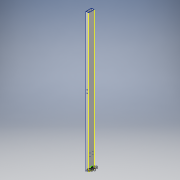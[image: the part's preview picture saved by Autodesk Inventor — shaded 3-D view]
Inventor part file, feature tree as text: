
AUTODESK INVENTOR PART (.ipt)
format: ipt  version: 2017 (Build 210142000, 142)  size: 151,552 bytes
history: native  units: in
note: dims shown in document units (in); Inventor stores cm internally (conversion verified against a paired STEP export)
features: sketch x6, extrude x3, hole x2
ambient origin geometry x8: Origin, YZ Plane, XZ Plane, XY Plane, X Axis, Y Axis, Z Axis, Center Point
bodies: Solid1 (feature_tree)
feature tree (11):
  extrude  "Extrusion1"  Depth=2.0in
  extrude  "Extrusion2"  Depth=1.75in
  extrude  "Extrusion3"  Depth=0.125in
  hole  "Hole1"  [1 undecoded]
  sketch  "Sketch6"  dims[d11=24.0in d12=0.5in]
  hole  "Hole3"  [1 undecoded]
  sketch  "Sketch2"  dims[d2=1.0in d3=2.0in]
  sketch  "Sketch3"  dims[d4=0.75in d5=1.75in]
  sketch  "Sketch4"  dims[d6=0.125in d7=0.125in]
  sketch  "Sketch5"  dims[d8=48.0in d9=0.0in d10=48.0in]
  sketch  "Sketch7"  dims[d13=0.25in d14=48.0in d15=0.0in d16=1.125in d17=1.125in d18=0.25in d19=0.0in d20=4.5in d21=0.5in d22=0.125in d24=0.125in d25=0.75in d26=0.375in d27=0.25in d28=0.5635in d29=0.125in d30=0.8108in d31=0.4375in d32=0.4375in d33=0.75in d41=1.125in d42=0.75in d43=0.375in d44=0.25in d45=0.5635in d46=0.125in d47=0.8108in]
note: 2 required parameter values undecoded (feature->parameter linkage not recoverable at this tier; creation-order binding heuristic only, values carry confidence <= 0.55)
